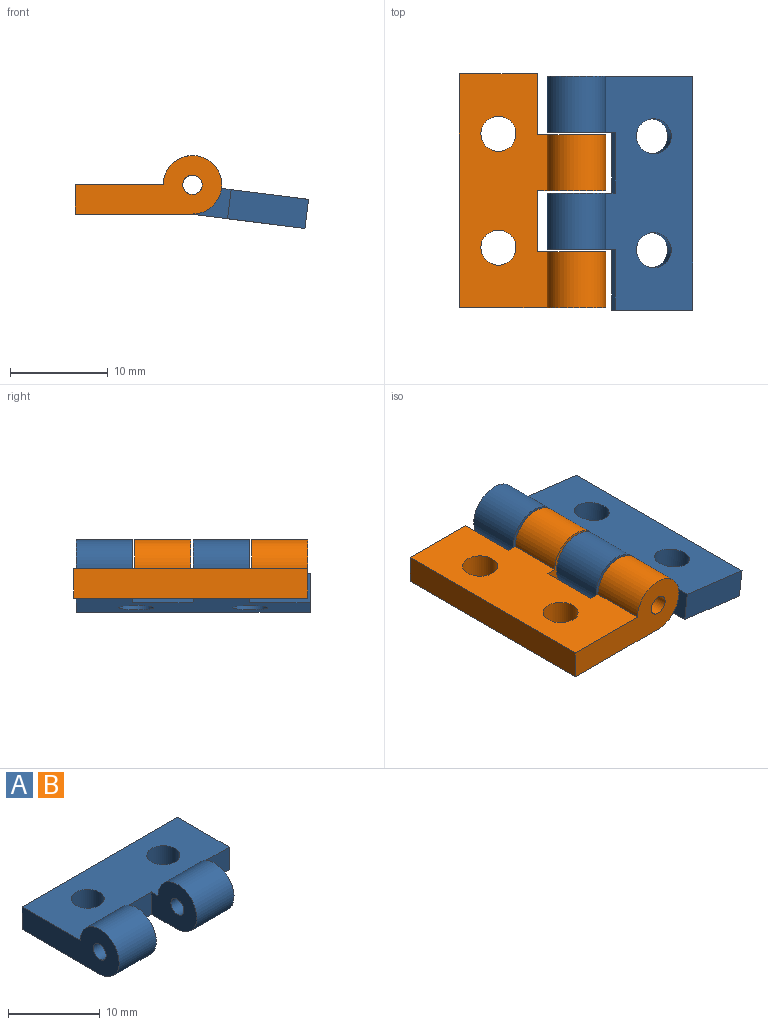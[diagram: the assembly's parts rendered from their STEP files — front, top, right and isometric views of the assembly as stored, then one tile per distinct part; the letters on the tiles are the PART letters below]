
ASSEMBLY  parts=2 mates=1
PART A: 16 faces, bbox 24x15x6 mm
  f0: plane 6.25x3mm, normal (0,-1,0), area 18.8mm2, adj f5,f6,f9,f13
  f1: plane 24x3mm, normal (0,1,0), area 72mm2, adj f2,f4,f5,f6
  f2: plane 15x6mm, normal (-1,0,0), area 54.1mm2, adj f1,f5,f6,f7,f8
  f3: plane 6.25x3mm, normal (0,-1,0), area 18.8mm2, adj f4,f5,f6,f12
  f4: plane 8x3mm, normal (1,0,0), area 24mm2, adj f1,f3,f5,f6
  f5: plane 24x9mm, normal (0,0,1), area 183.1mm2, adj f0,f1,f2,f3,f4,f7,f9,f10
  f6: plane 24x12mm, normal (0,0,-1), area 217.6mm2, adj f0,f1,f2,f3,f4,f7,f9,f10
  f7: cylinder r=3mm len=6mm, axis (-1,0,0), area 81.3mm2, adj f2,f5,f6,f9
  f8: cylinder r=1mm len=5.75mm, axis (-1,0,0), area 36.1mm2, adj f2,f9
  f9: plane 7x6mm, normal (1,0,0), area 30.1mm2, adj f0,f5,f6,f7,f8
  f10: cylinder r=3mm len=6mm, axis (-1,0,0), area 81.3mm2, adj f5,f6,f12,f13
  f11: cylinder r=1mm len=5.75mm, axis (-1,0,0), area 36.1mm2, adj f12,f13
  f12: plane 7x6mm, normal (1,0,0), area 30.1mm2, adj f3,f5,f6,f10,f11
  f13: plane 7x6mm, normal (-1,0,0), area 30.1mm2, adj f0,f5,f6,f10,f11
  f14: cylinder r=1.8mm len=3.6mm, axis (0,0,1), area 33.9mm2, adj f5,f6
  f15: cylinder r=1.8mm len=3.6mm, axis (0,0,1), area 33.9mm2, adj f5,f6
PART B: same geometry as A
PLACE A rot(axis=(-0.06,0.06,-1),90.2deg) t=(10.74,-12.25,0.13)mm
PLACE B rot(axis=(0,0,1),90deg) t=(12.89,-12,0)mm
MATE revolute A.f7 <-> B.f7  axis (0,-1,0) through (12,-18,3)mm
